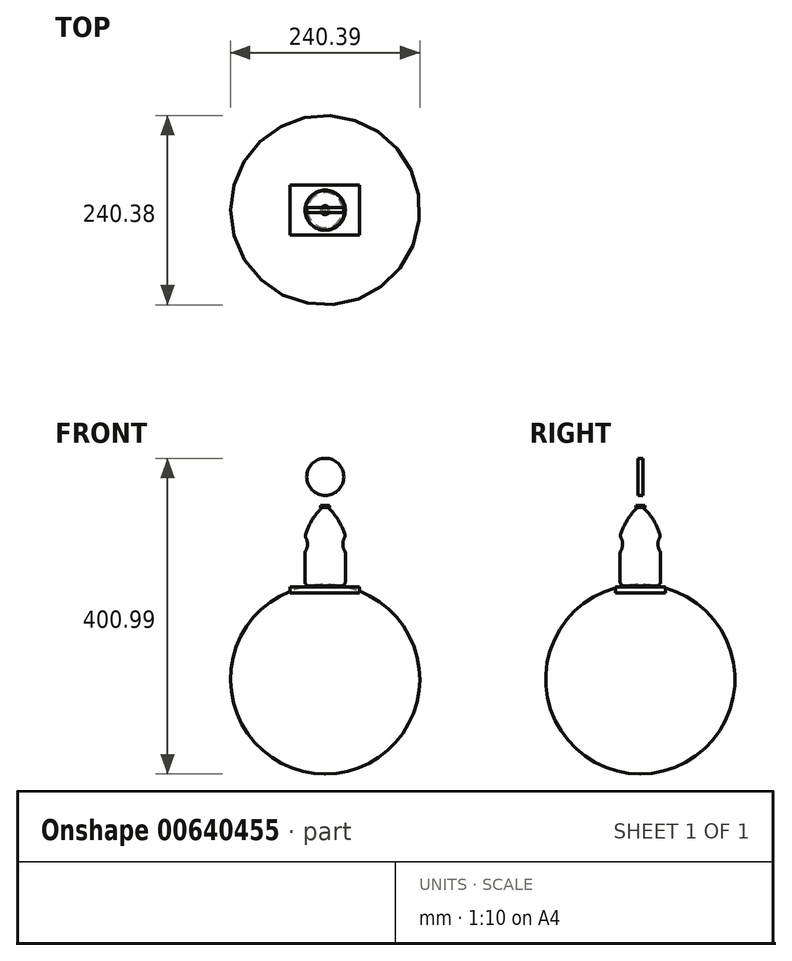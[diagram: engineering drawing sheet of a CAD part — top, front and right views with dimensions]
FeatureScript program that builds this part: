
annotation { "Feature Type Name" : "Feature", "Feature Type Description" : "" }
export const myFeature = defineFeature(function(context is Context, id is Id, definition is map)
    precondition{}
    {
        {
            var Q0;
            Q0=qCreatedBy(makeId("Front.planeOp"),FACE);
            var sketch = newSketch(context, id + "F0", { "sketchPlane" : qUnion([Q0])});
            skLineSegment(sketch, "E0", {"start": v(150.9, 103.13) * mm, "end": v(145.2, 103.13) * mm});
            skLineSegment(sketch, "E1", {"start": v(145.2, 103.13) * mm, "end": v(145.2, 100.6) * mm});
            skLineSegment(sketch, "E2", {"start": v(145.2, 100.6) * mm, "end": v(147.24, 100.6) * mm});
            skArc(sketch, "E3", {"start": v(150.9, 2.73) * mm, "mid": v(138.03, 2.05) * mm, "end": v(125.3, 0) * mm});
            skArc(sketch, "E4", {"start": v(147.24, 100.6) * mm, "mid": v(133.75, 83.76) * mm, "end": v(125.3, 63.92) * mm});
            skArc(sketch, "E5", {"start": v(125.3, 44.4) * mm, "mid": v(128.5, 54.16) * mm, "end": v(125.3, 63.92) * mm});
            skLineSegment(sketch, "E6", {"start": v(125.3, 44.4) * mm, "end": v(125.3, 0) * mm});
            skLineSegment(sketch, "E7", {"start": v(150.9, 103.13) * mm, "end": v(150.9, 2.73) * mm});
            skSolve(sketch);
        }
        {
            var Q0;
            Q0=makeQuery(id+"F0.imprint","IMPRINT",FACE,{"disambiguationData":[TD([[makeQuery(id+"F0.imprint","IMPRINT",EDGE,{"derivedFrom":sQuery(id+"F0.wireOp",EDGE,"E0")}),1.0]])]});
            var Q1;
            Q1=sQuery(id+"F0.wireOp",EDGE,"E7");
            revolve(context, id + "F1", {"entities" : qUnion([Q0]), "axis" : qUnion([Q1]), "revolveType" : RevolveType.FULL});
        }
        {
            var Q0;
            Q0=makeQuery(id+"F1.opRevolve","SWEPT_EDGE",EDGE,{"disambiguationData":[OSD([sQuery(id+"F0.wireOp",EDGE,"E4"),sQuery(id+"F0.wireOp",EDGE,"E5")])]});
            var Q1;
            Q1=makeQuery(id+"F1.opRevolve","SWEPT_EDGE",EDGE,{"disambiguationData":[OSD([sQuery(id+"F0.wireOp",EDGE,"E5"),sQuery(id+"F0.wireOp",EDGE,"E6")])]});
            var Q2;
            Q2=makeQuery(id+"F1.opRevolve","SWEPT_EDGE",EDGE,{"disambiguationData":[OSD([sQuery(id+"F0.wireOp",EDGE,"E3"),sQuery(id+"F0.wireOp",EDGE,"E6")])]});
            fillet(context, id + "F2", {"entities" : qUnion([Q0, Q1, Q2]), "radius" : 5.08 * mm, "tangentPropagation" : true, "allowEdgeOverflow" : false});
        }
        {
            var Q0;
            Q0=qCreatedBy(makeId("Front.planeOp"),FACE);
            var sketch = newSketch(context, id + "F3", { "sketchPlane" : qUnion([Q0])});
            skCircle(sketch, "E8", {"center": v(151.1, 139.54) * mm, "radius": 23.6 * mm});
            skSolve(sketch);
        }
        {
            var Q0;
            Q0=makeQuery(id+"F3.imprint","IMPRINT",FACE,{"disambiguationData":[TD([[makeQuery(id+"F3.imprint","IMPRINT",EDGE,{"derivedFrom":sQuery(id+"F3.wireOp",EDGE,"E8")}),1.0]])]});
            extrude(context, id + "F4", {"entities" : qUnion([Q0]), "endBound" : BoundingType.SYMMETRIC, "depth" : 6.35 * mm, "offsetDistance" : 25.4 * mm});
        }
        {
            var Q0;
            Q0=qCreatedBy(makeId("Front.planeOp"),FACE);
            var sketch = newSketch(context, id + "F5", { "sketchPlane" : qUnion([Q0])});
            skLineSegment(sketch, "E9", {"start": v(168.56, 0) * mm, "end": v(194.37, 0) * mm});
            skLineSegment(sketch, "E10", {"start": v(194.37, 0) * mm, "end": v(194.37, -8.17) * mm});
            skLineSegment(sketch, "E11", {"start": v(194.37, -8.17) * mm, "end": v(106.13, -8.17) * mm});
            skLineSegment(sketch, "E12", {"start": v(106.13, -8.17) * mm, "end": v(106.13, 0) * mm});
            skLineSegment(sketch, "E13", {"start": v(106.13, 0) * mm, "end": v(168.56, 0) * mm});
            skSolve(sketch);
        }
        {
            var Q0;
            Q0=makeQuery(id+"F5.imprint","IMPRINT",FACE,{"disambiguationData":[TD([[makeQuery(id+"F5.imprint","IMPRINT",EDGE,{"derivedFrom":sQuery(id+"F5.wireOp",EDGE,"E9")}),-1.0]])]});
            extrude(context, id + "F6", {"entities" : qUnion([Q0]), "endBound" : BoundingType.SYMMETRIC, "depth" : 63.5 * mm, "offsetDistance" : 25.4 * mm});
        }
        {
            var Q0;
            Q0=makeQuery(id+"F6.opExtrude","CAP_EDGE",EDGE,{"disambiguationData":[OSD([sQuery(id+"F5.wireOp",EDGE,"E9"),sQuery(id+"F5.wireOp",EDGE,"E13")])],"isStart":false});
            cPoint(context, id + "F7", {"entities" : qUnion([Q0]), "parameter" : 0.5});
        }
        {
            var Q0;
            Q0=qCreatedBy(makeId("Right.planeOp"),FACE);
            var Q1;
            Q1 = qCreatedBy(id + "F7" ,VERTEX);
            cPlane(context, id + "F8", {"entities" : qUnion([Q0, Q1]), "cplaneType" : CPlaneType.PLANE_POINT, "offset" : 84.58 * mm, "width" : 152.4 * mm, "height" : 152.4 * mm});
        }
    });
